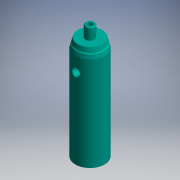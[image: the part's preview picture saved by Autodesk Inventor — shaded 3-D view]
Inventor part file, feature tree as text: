
AUTODESK INVENTOR PART (.ipt)
format: ipt  version: 2016 (Build 200138000, 138)  size: 215,040 bytes
history: native  units: mm (DEFAULTED — no unit token found)
features: other x2, extrude x1, sketch x1
ambient origin geometry x8: Origin, YZ Plane, XZ Plane, XY Plane, X Axis, Y Axis, Z Axis, Center Point
bodies: Solid1 (feature_tree), Solid2 (feature_tree)
feature tree (4):
  extrude  "Extrusion1"  [1 undecoded]
  sketch  "Sketch1"  dims[d0=5.2mm d1=0.0mm]
  other  "0331-001-1-solid1"
  other  "21110-001-1-solid1"
note: 1 required parameter value undecoded (feature->parameter linkage not recoverable at this tier; creation-order binding heuristic only, values carry confidence <= 0.55)
